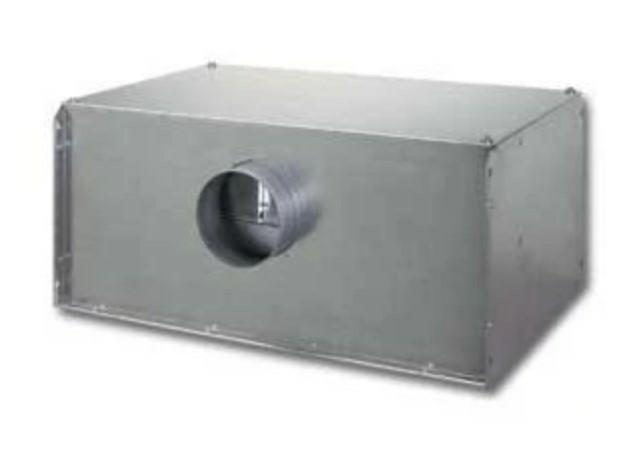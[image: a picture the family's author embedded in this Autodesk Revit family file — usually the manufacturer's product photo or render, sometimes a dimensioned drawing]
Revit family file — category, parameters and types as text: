
# Revit family: CADS_Vent-Axia_MechEquip_Fan_QPTW_QuietPackTwin - EXTRACT
name_source: partatom
category: Mechanical Equipment
units: mm (PartAtom-declared; Revit-internal decimal feet)

## family parameters
Classification = None
Cut with Voids When Loaded = No
Host = Face
OmniClass Number = 23.75.35.17.11
OmniClass Title = Fans for Air Ductwork
Part Type = Normal
Room Calculation Point = No
Round Connector Dimension = Use Diameter
Shared = No

## types (7) — shared parameters
Air Flow = 0.0 L/s
AirflowRateRange = 0.0 L/s
AssemblyPlace = UNKNOWN
AssetType = FIXED
Default Elevation = 1219 mm
DurationUnit = Year
EBHoffset = 206 mm
EBVoffset = 80 mm
ExteriorInsulation = No
Fitting Type = Ignore
GrossWeight = 0.00 kg
HasProtectiveEarth = No
IsExtendedWarranty = No
ManufacturerAddress = Fleming Way
Crawley 
RH10 9YX
Quantity = 1
RatedCurrent = 0 A
RatedVoltage = 0 V
Status = New
WarrantyGuarantor = Vent-Axia Limited
WorkingPressure = 0.0 Pa
zero-valued in all types: CADS_Index, CADS_Usage, ExpectedServiceLife, H, NumberOfPoles, OutOffset, W

## per-type parameters (varying)
| type | L | ModelReference | NominalDiameter | NominalHeight | NominalLength | NominalWidth | SpigotCLHeight | Type Image |
| QPTW100C | 590 mm  [stored 1.9357 ft] | QPTW100C QUIET PACK TWIN FAN | 100 mm  [stored 0.328084 ft] | 256 mm  [stored 0.839895 ft] | 610 mm  [stored 2.00131 ft] | 622 mm  [stored 2.04068 ft] | 128 mm  [stored 0.419948 ft] | <None> |
| QPTW125C | 590 mm  [stored 1.9357 ft] | QPTW125C QUIET PACK TWIN FAN | 125 mm  [stored 0.410105 ft] | 256 mm  [stored 0.839895 ft] | 610 mm  [stored 2.00131 ft] | 622 mm  [stored 2.04068 ft] | 128 mm  [stored 0.419948 ft] | <None> |
| QPTW150C | 590 mm  [stored 1.9357 ft] | QPTW150C QUIET PACK TWIN FAN | 150 mm | 256 mm  [stored 0.839895 ft] | 610 mm  [stored 2.00131 ft] | 622 mm  [stored 2.04068 ft] | 128 mm  [stored 0.419948 ft] | <None> |
| QPTW160C | 590 mm  [stored 1.9357 ft] | QPTW160C QUIET PACK TWIN FAN | 160 mm  [stored 0.524934 ft] | 256 mm  [stored 0.839895 ft] | 610 mm  [stored 2.00131 ft] | 622 mm  [stored 2.04068 ft] | 128 mm  [stored 0.419948 ft] | <None> |
| QPTW250C | 905 mm  [stored 2.96916 ft] | QPTW250C QUIET PACK TWIN FAN | 250 mm  [stored 0.82021 ft] | 354 mm  [stored 1.16142 ft] | 925 mm  [stored 3.03478 ft] | 829 mm  [stored 2.71982 ft] | 177 mm  [stored 0.580709 ft] | <None> |
| QPTW315C | 1235 mm  [stored 4.05184 ft] | QPTW315C QUIET PACK TWIN FAN | 315 mm  [stored 1.03346 ft] | 536 mm  [stored 1.75853 ft] | 1255 mm  [stored 4.11745 ft] | 1176 mm  [stored 3.85827 ft] | 268 mm | <None> |
| QPTW400C | 1235 mm  [stored 4.05184 ft] | QPTW400C QUIET PACK TWIN FAN | 400 mm  [stored 1.31234 ft] | 536 mm  [stored 1.75853 ft] | 1255 mm  [stored 4.11745 ft] | 1176 mm  [stored 3.85827 ft] | 268 mm | CADS_Vent-Axia_MechEquip_Fan_QPTW_QuietPackTwin.jpg |

note: column(s) folded — value = type name in every type: ModelNumber

note: [stored X ft] marks values corroborated as IEEE doubles in the binary element streams (Revit-internal decimal feet)

## geometry (parser evidence)
native form markers: Sweep x4
no freeform markers — native parametric forms only
